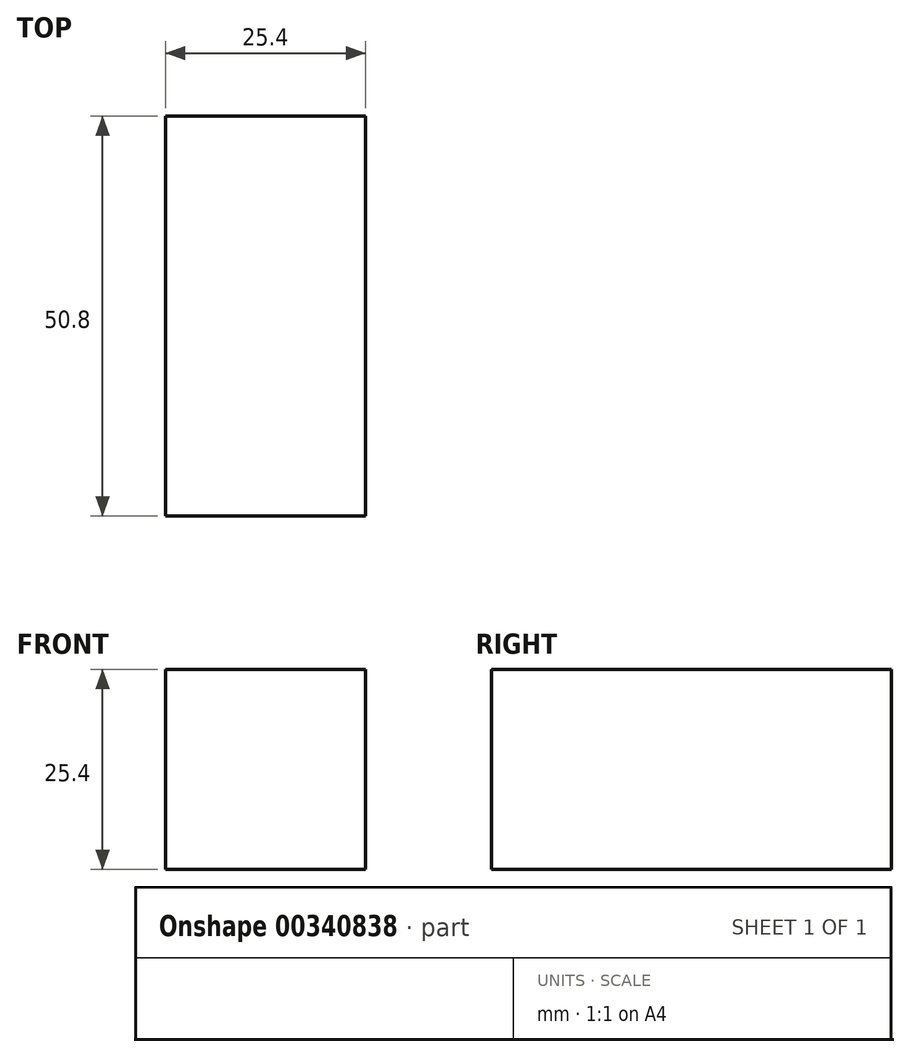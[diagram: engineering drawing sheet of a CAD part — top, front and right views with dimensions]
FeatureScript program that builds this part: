
annotation { "Feature Type Name" : "Feature", "Feature Type Description" : "" }
export const myFeature = defineFeature(function(context is Context, id is Id, definition is map)
    precondition{}
    {
        {
            var Q0;
            Q0=qCreatedBy(makeId("Right.planeOp"),FACE);
            var sketch = newSketch(context, id + "F0", { "sketchPlane" : qUnion([Q0])});
            skLineSegment(sketch, "E0.bottom", {"start": v(0, 0) * mm, "end": v(50.8, 0) * mm});
            skLineSegment(sketch, "E0.top", {"start": v(0, 25.4) * mm, "end": v(50.8, 25.4) * mm});
            skLineSegment(sketch, "E0.left", {"start": v(0, 0) * mm, "end": v(0, 25.4) * mm});
            skLineSegment(sketch, "E0.right", {"start": v(50.8, 0) * mm, "end": v(50.8, 25.4) * mm});
            skSolve(sketch);
        }
        {
            var Q0;
            Q0 = qSketchRegion(id + "F0", true);
            extrude(context, id + "F1", {"entities" : qUnion([Q0]), "depth" : 25.4 * mm});
        }
    });
